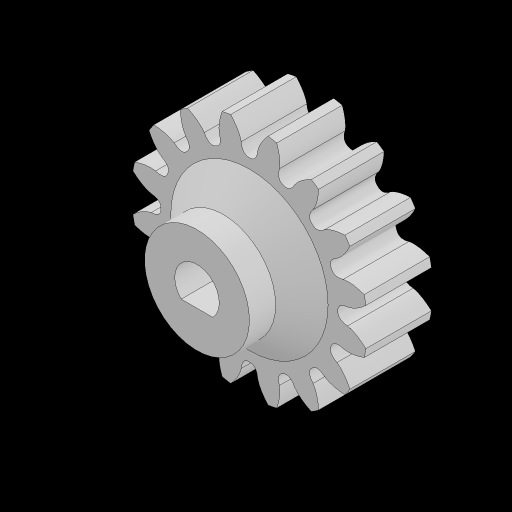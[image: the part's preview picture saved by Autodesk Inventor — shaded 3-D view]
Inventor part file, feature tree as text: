
AUTODESK INVENTOR PART (.ipt)
format: ipt  version: 2023.2 (Build 272271030, 271C)  size: 344,064 bytes
history: native  units: mm
features: extrude x4, sketch x3, pattern_circular x1, chamfer x1, projected_geometry x1
ambient origin geometry x8: Origin, YZ Plane, XZ Plane, XY Plane, X Axis, Y Axis, Z Axis, Center Point
bodies: Solid1 (feature_tree)
feature tree (10):
  sketch  "Sketch1"  dims[d0=5.0mm d1=0.0mm d2=0.0mm d3=0.0mm]
  extrude  "Extrusion1"  TaperAngle=0.0deg  [1 undecoded]
  extrude  "Extrusion2"  Depth=3.0mm
  pattern_circular  "Circular Pattern1"  [2 undecoded]
  extrude  "Extrusion3"  TaperAngle=0.0deg  [1 undecoded]
  extrude  "Extrusion4"  Depth=4.0mm
  chamfer  "Chamfer1"  Distance=4.0mm
  sketch  "Sketch2"  dims[d4=160.0mm d5=360.0deg d7=3.0mm]
  sketch  "Sketch3"  dims[d8=2.5mm d9=0.2mm d10=0.0mm d11=0.0mm d12=8.0mm d13=4.0mm d14=0.0mm d15=2.0mm d16=2.0mm d17=45.0deg]
  projected_geometry  "Projected Loop1"
note: 4 required parameter values undecoded (feature->parameter linkage not recoverable at this tier; creation-order binding heuristic only, values carry confidence <= 0.55)
